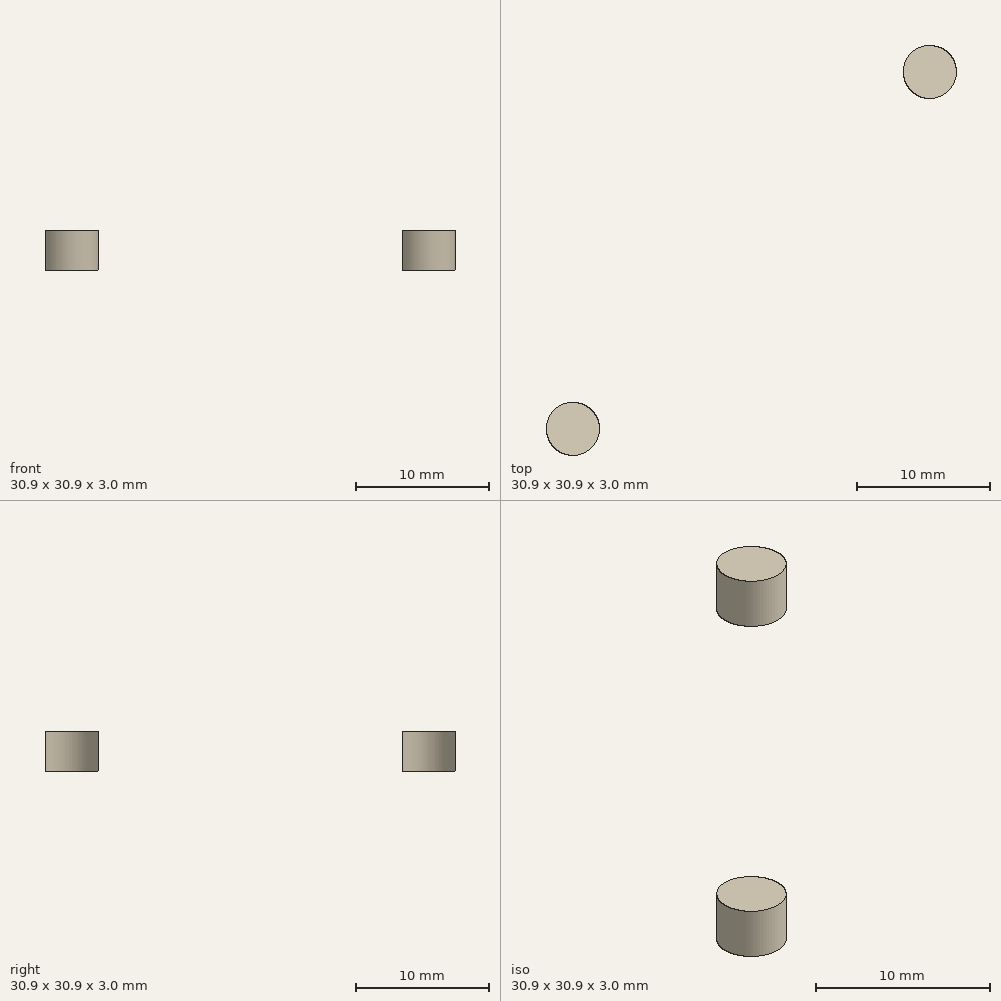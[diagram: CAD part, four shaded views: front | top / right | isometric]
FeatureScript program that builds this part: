
annotation { "Feature Type Name" : "Feature", "Feature Type Description" : "" }
export const myFeature = defineFeature(function(context is Context, id is Id, definition is map)
    precondition{}
    {
        {
            var Q0;
            Q0=qCreatedBy(makeId("Top.planeOp"),FACE);
            var sketch = newSketch(context, id + "F0", { "sketchPlane" : qUnion([Q0])});
            skLineSegment(sketch, "E0.bottom", {"start": v(5, 32.5) * mm, "end": v(-5, 32.5) * mm});
            skLineSegment(sketch, "E0.top", {"start": v(5, -32.5) * mm, "end": v(-5, -32.5) * mm});
            skLineSegment(sketch, "E0.left", {"start": v(20, 17.5) * mm, "end": v(20, 15.45) * mm});
            skLineSegment(sketch, "E0.right", {"start": v(-20, 17.5) * mm, "end": v(-20, 15.45) * mm});
            skPoint(sketch, "E0.middle", {"position": v(0, 0) * mm});
            skArc(sketch, "E1", {"start": v(3, -2.2) * mm, "mid": v(0, 27.5) * mm, "end": v(-3, -2.2) * mm});
            skCircle(sketch, "E2", {"center": v(0, -17.5) * mm, "radius": 4.03 * mm});
            skPoint(sketch, "E3.visualSharp", {"position": v(-20, 32.5) * mm});
            skArc(sketch, "E3.filletArc", {"start": v(-5, 32.5) * mm, "mid": v(-15.6, 28.1) * mm, "end": v(-20, 17.5) * mm});
            skPoint(sketch, "E4.visualSharp", {"position": v(20, 32.5) * mm});
            skArc(sketch, "E4.filletArc", {"start": v(20, 17.5) * mm, "mid": v(15.6, 28.1) * mm, "end": v(5, 32.5) * mm});
            skPoint(sketch, "E5.visualSharp", {"position": v(-20, -32.5) * mm});
            skArc(sketch, "E5.filletArc", {"start": v(-20, -17.5) * mm, "mid": v(-15.6, -28.1) * mm, "end": v(-5, -32.5) * mm});
            skPoint(sketch, "E6.visualSharp", {"position": v(20, -32.5) * mm});
            skArc(sketch, "E6.filletArc", {"start": v(5, -32.5) * mm, "mid": v(15.6, -28.1) * mm, "end": v(20, -17.5) * mm});
            skLineSegment(sketch, "E7", {"start": v(-3, -2.2) * mm, "end": v(-3, -1.4) * mm});
            skLineSegment(sketch, "E8", {"start": v(3, -1.4) * mm, "end": v(3, -2.2) * mm});
            skArc(sketch, "E9.0", {"start": v(-2.88, -1.3) * mm, "mid": v(0, -1.6) * mm, "end": v(2.88, -1.3) * mm});
            skPoint(sketch, "E10.visualSharp", {"position": v(-3, -1.28) * mm});
            skArc(sketch, "E10.filletArc", {"start": v(-2.88, -1.3) * mm, "mid": v(-2.96, -1.32) * mm, "end": v(-3, -1.4) * mm});
            skPoint(sketch, "E11.visualSharp", {"position": v(3, -1.28) * mm});
            skArc(sketch, "E11.filletArc", {"start": v(3, -1.4) * mm, "mid": v(2.96, -1.32) * mm, "end": v(2.88, -1.3) * mm});
            skLineSegment(sketch, "E12", {"start": v(-20, 15.45) * mm, "end": v(-17, 15.45) * mm, "construction": true});
            skLineSegment(sketch, "E13", {"start": v(-17, 15.45) * mm, "end": v(-17, -14.5) * mm, "construction": true});
            skLineSegment(sketch, "E14", {"start": v(-17, -14.5) * mm, "end": v(-20, -14.5) * mm, "construction": true});
            skLineSegment(sketch, "E15.trimOffspring", {"start": v(-20, -14.5) * mm, "end": v(-20, -17.5) * mm});
            skLineSegment(sketch, "E16", {"start": v(-20, 15.45) * mm, "end": v(-20, -14.5) * mm});
            skLineSegment(sketch, "E17.MirrorCS", {"start": v(17, -14.5) * mm, "end": v(20, -14.5) * mm, "construction": true});
            skLineSegment(sketch, "E18.MirrorCS", {"start": v(17, 15.45) * mm, "end": v(17, -14.5) * mm, "construction": true});
            skLineSegment(sketch, "E19.MirrorCS", {"start": v(20, 15.45) * mm, "end": v(17, 15.45) * mm, "construction": true});
            skLineSegment(sketch, "E20", {"start": v(17, -14.5) * mm, "end": v(17, 15.45) * mm, "construction": true});
            skLineSegment(sketch, "E21", {"start": v(17, 15.45) * mm, "end": v(17, -14.5) * mm});
            skLineSegment(sketch, "E22", {"start": v(20, -14.5) * mm, "end": v(17, -14.5) * mm});
            skLineSegment(sketch, "E23", {"start": v(20, 15.45) * mm, "end": v(17, 15.45) * mm});
            skLineSegment(sketch, "E24.trimOffspring", {"start": v(20, -14.5) * mm, "end": v(20, -17.5) * mm});
            skSolve(sketch);
        }
        {
            var Q0;
            Q0=makeQuery(id+"F0.imprint","IMPRINT",FACE,{"disambiguationData":[TD([[makeQuery(id+"F0.imprint","IMPRINT",EDGE,{"derivedFrom":sQuery(id+"F0.wireOp",EDGE,"E0.bottom")}),1.0]])]});
            extrude(context, id + "F1", {"entities" : qUnion([Q0]), "depth" : 3 * mm, "offsetDistance" : 25 * mm});
        }
        {
            var Q0;
            Q0=makeQuery(id+"F1.opExtrude","CAP_FACE",FACE,{"disambiguationData":[OSD([sQuery(id+"F0.wireOp",EDGE,"E0.bottom"),sQuery(id+"F0.wireOp",EDGE,"E0.top"),sQuery(id+"F0.wireOp",EDGE,"E0.left"),sQuery(id+"F0.wireOp",EDGE,"E0.right"),sQuery(id+"F0.wireOp",EDGE,"E1"),sQuery(id+"F0.wireOp",EDGE,"E2"),sQuery(id+"F0.wireOp",EDGE,"E3.filletArc"),sQuery(id+"F0.wireOp",EDGE,"E4.filletArc"),sQuery(id+"F0.wireOp",EDGE,"E5.filletArc"),sQuery(id+"F0.wireOp",EDGE,"E6.filletArc"),sQuery(id+"F0.wireOp",EDGE,"E7"),sQuery(id+"F0.wireOp",EDGE,"E8"),sQuery(id+"F0.wireOp",EDGE,"E9.0"),sQuery(id+"F0.wireOp",EDGE,"E10.filletArc"),sQuery(id+"F0.wireOp",EDGE,"E11.filletArc")])],"isStart":false});
            var sketch = newSketch(context, id + "F2", { "sketchPlane" : qUnion([Q0])});
            skLineSegment(sketch, "E25", {"start": v(0, 12.5) * mm, "end": v(-15.6, 28.1) * mm, "construction": true});
            skLineSegment(sketch, "E26", {"start": v(0, 12.5) * mm, "end": v(-20, 12.5) * mm, "construction": true});
            skCircle(sketch, "E27", {"center": v(-13.44, 25.94) * mm, "radius": 2 * mm});
            skCircle(sketch, "E28.MirrorC", {"center": v(-13.44, -0.94) * mm, "radius": 2 * mm});
            skCircle(sketch, "E29.MirrorC", {"center": v(13.44, 25.94) * mm, "radius": 2 * mm});
            skCircle(sketch, "E30.MirrorC", {"center": v(13.44, -0.94) * mm, "radius": 2 * mm});
            skSolve(sketch);
        }
        {
            var Q0;
            Q0=makeQuery(id+"F2.imprint","IMPRINT",FACE,{"disambiguationData":[TD([[makeQuery(id+"F2.imprint","IMPRINT",EDGE,{"derivedFrom":sQuery(id+"F2.wireOp",EDGE,"E27")}),1.0]])]});
            var Q1;
            Q1=makeQuery(id+"F2.imprint","IMPRINT",FACE,{"disambiguationData":[TD([[makeQuery(id+"F2.imprint","IMPRINT",EDGE,{"derivedFrom":sQuery(id+"F2.wireOp",EDGE,"E29.MirrorC")}),-1.0]])]});
            var Q2;
            Q2=makeQuery(id+"F2.imprint","IMPRINT",FACE,{"disambiguationData":[TD([[makeQuery(id+"F2.imprint","IMPRINT",EDGE,{"derivedFrom":sQuery(id+"F2.wireOp",EDGE,"E28.MirrorC")}),-1.0]])]});
            var Q3;
            Q3=makeQuery(id+"F2.imprint","IMPRINT",FACE,{"disambiguationData":[TD([[makeQuery(id+"F2.imprint","IMPRINT",EDGE,{"derivedFrom":sQuery(id+"F2.wireOp",EDGE,"E30.MirrorC")}),1.0]])]});
            extrude(context, id + "F3", {"entities" : qUnion([Q0, Q1, Q2, Q3]), "operationType" : NewBodyOperationType.REMOVE, "oppositeDirection" : true, "depth" : 25 * mm, "offsetDistance" : 25 * mm});
        }
    });
